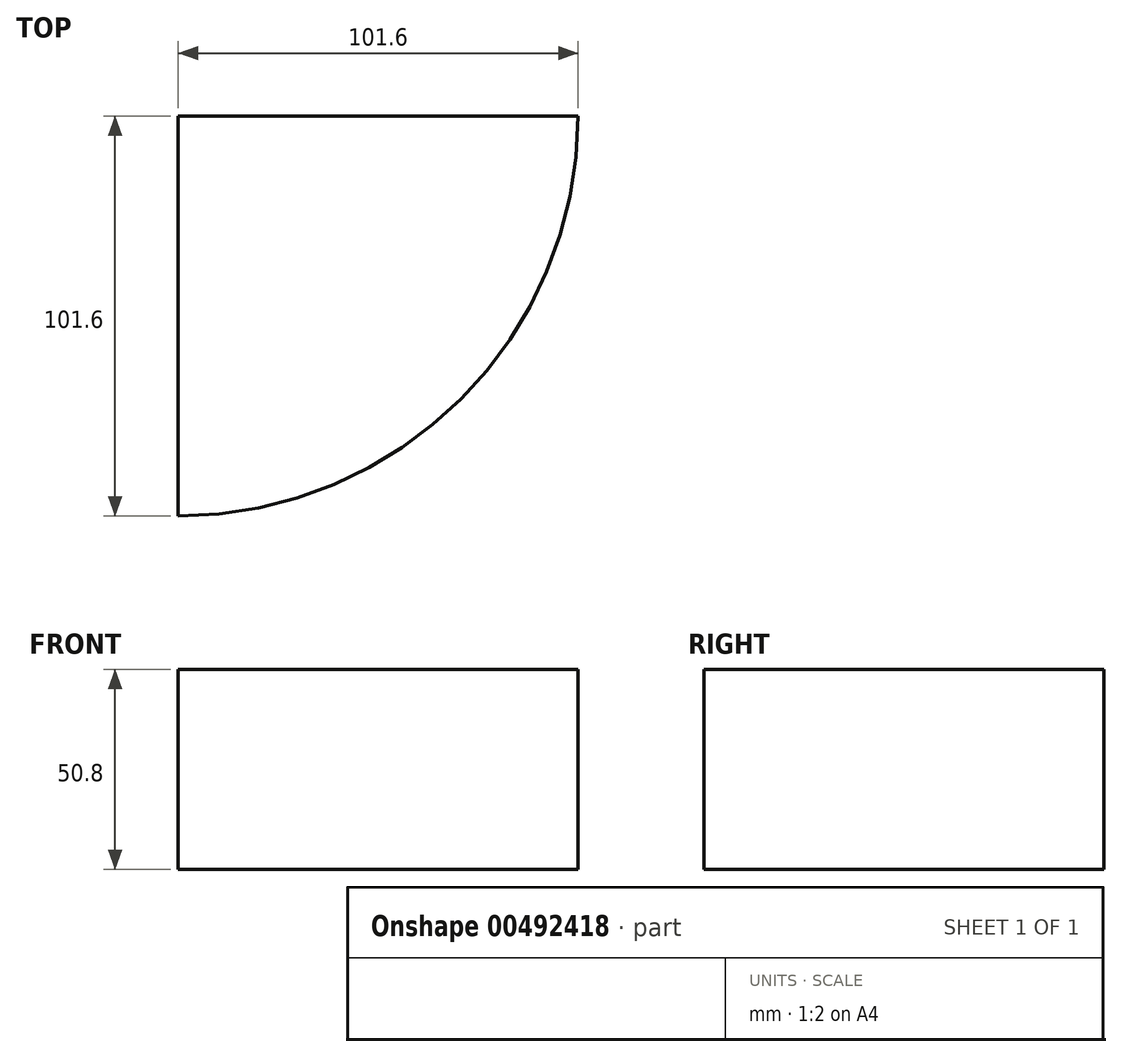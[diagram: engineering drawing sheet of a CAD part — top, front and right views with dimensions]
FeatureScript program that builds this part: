
annotation { "Feature Type Name" : "Feature", "Feature Type Description" : "" }
export const myFeature = defineFeature(function(context is Context, id is Id, definition is map)
    precondition{}
    {
        {
            var Q0;
            Q0=qCreatedBy(makeId("Front.planeOp"),FACE);
            var sketch = newSketch(context, id + "F0", { "sketchPlane" : qUnion([Q0])});
            skLineSegment(sketch, "E0.bottom", {"start": v(0, 0) * mm, "end": v(101.6, 0) * mm});
            skLineSegment(sketch, "E0.top", {"start": v(0, -50.8) * mm, "end": v(101.6, -50.8) * mm});
            skLineSegment(sketch, "E0.left", {"start": v(0, 0) * mm, "end": v(0, -50.8) * mm});
            skLineSegment(sketch, "E0.right", {"start": v(101.6, 0) * mm, "end": v(101.6, -50.8) * mm});
            skSolve(sketch);
        }
        {
            var Q0;
            Q0=makeQuery(id+"F0.imprint","IMPRINT",FACE,{"disambiguationData":[TD([[makeQuery(id+"F0.imprint","IMPRINT",EDGE,{"derivedFrom":sQuery(id+"F0.wireOp",EDGE,"E0.bottom")}),-1.0]])]});
            var Q1;
            Q1=sQuery(id+"F0.wireOp",EDGE,"E0.left");
            revolve(context, id + "F1", {"entities" : qUnion([Q0]), "axis" : qUnion([Q1]), "revolveType" : RevolveType.ONE_DIRECTION, "angle" : 90 * degree});
        }
    });
